# Revit family: Deca_Saboneteira de parede_Disco_2010.DSC
name_source: partatom
category: Plumbing Fixtures
units: mm (PartAtom-declared; Revit-internal decimal feet)

## family parameters
Cut with Voids When Loaded = No
Host = Face
Part Type = Normal
Room Calculation Point = No
Round Connector Dimension = Use Diameter
Shared = No

## types (3) — shared parameters
Acompanha o Produto = Acompanha Parafusos e Buchas para fixação para alvenaria
Aprovado por = quattroD
Atendimento ao Cliente = 0800-0117073
Categoria = ACESSORIOS
Composição Anel Vedação = -
Composição Assento = -
Composição Básica = Liga de Cobre (bronze e latão),Plásticos de Engenharia
Composição Componente = -
Consumo = -
Cor Interna = -
Cor Secundária = Translúcida
Cores Componente = -
Criado por = quattroD
Código Pai = 2010.DSC
Default Elevation = 1100 mm
Description = Saboneteira de parede
Informações Complementares = -
Itens de Instalação = -
Linha = Acessório Disco
Manufacturer = Deca
Material Secundário = Deca_Translúcido (Resina)
Norma = Não Possui
Pressão máx. funcionamento = -
Pressão mín. Aquec. Acúmulo = -
Pressão mín. Aquec. Passagem = -
Pressão mín. funcionamento = -
Saída de Esgoto = -
Segmento = Banheiro Médio
Tipo de dispositivo economizador = -
Tipo de mecanismo utilizado = -
Tipo de rosca de entrada = -
Tipo de rosca de saída = -
URL = www.deca.com.br
Vazão na Pressão máx. (L/min) = -
Vazão na Pressão mín. (L/min) = -
zero-valued in all types: HWFU

## per-type parameters (varying)
| type | Cor Principal | Material | Model | Peso Líquido (Kg) |
| 2010.C.DSC_Cromado | Cromado | Deca_Cromado | 2010.C.DSC | 0.369 |
| 2010.BL.DSC.NO_Black Noir | Black Noir | Deca_Black Noir | 2010.BL.DSC.NO | 0.369 |
| 2010.GL.DSC.RD_Red Gold | Red Gold | Deca_Red Gold | 2010.GL.DSC.RD | 0.394 |

## geometry (parser evidence)
native form markers: Sweep x2
no freeform markers — native parametric forms only
